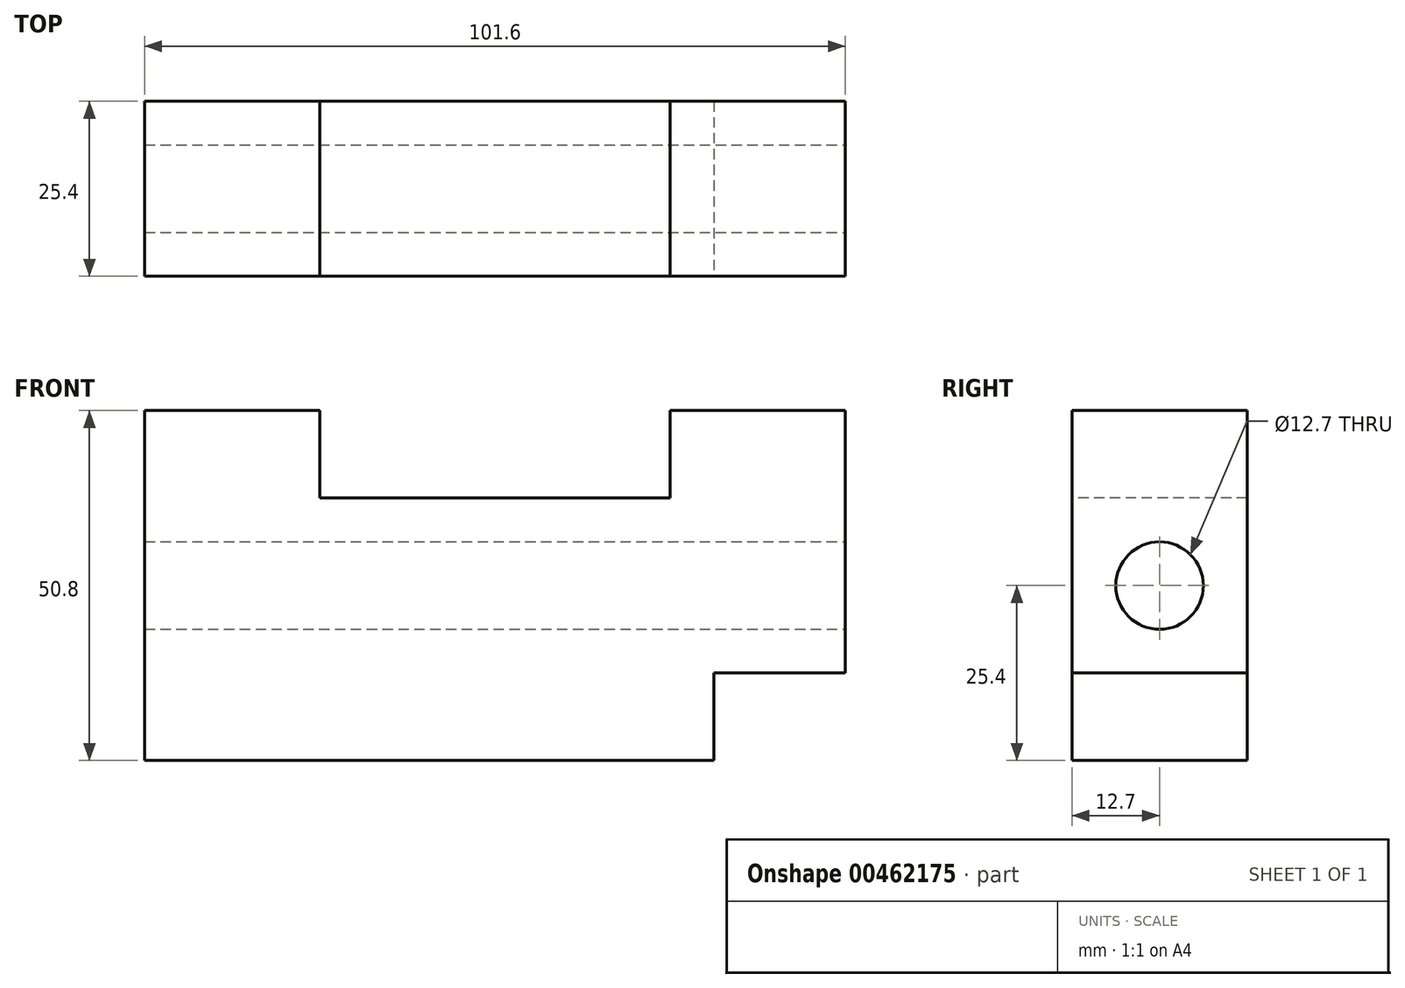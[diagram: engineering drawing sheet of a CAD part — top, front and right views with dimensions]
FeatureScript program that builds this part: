
annotation { "Feature Type Name" : "Feature", "Feature Type Description" : "" }
export const myFeature = defineFeature(function(context is Context, id is Id, definition is map)
    precondition{}
    {
        {
            var Q0;
            Q0=qCreatedBy(makeId("Front.planeOp"),FACE);
            var sketch = newSketch(context, id + "F0", { "sketchPlane" : qUnion([Q0])});
            skLineSegment(sketch, "E0.bottom", {"start": v(50.8, -25.4) * mm, "end": v(-50.8, -25.4) * mm});
            skLineSegment(sketch, "E0.top", {"start": v(50.8, 25.4) * mm, "end": v(-50.8, 25.4) * mm});
            skLineSegment(sketch, "E0.left", {"start": v(50.8, -25.4) * mm, "end": v(50.8, 25.4) * mm});
            skLineSegment(sketch, "E0.right", {"start": v(-50.8, -25.4) * mm, "end": v(-50.8, 25.4) * mm});
            skPoint(sketch, "E0.middle", {"position": v(0, 0) * mm});
            skSolve(sketch);
        }
        {
            var Q0;
            Q0 = qSketchRegion(id + "F0", true);
            extrude(context, id + "F1", {"entities" : qUnion([Q0]), "depth" : 25.4 * mm});
        }
        {
            var Q0;
            Q0=makeQuery(id+"F1.opExtrude","CAP_FACE",FACE,{"disambiguationData":[OSD([sQuery(id+"F0.wireOp",EDGE,"E0.bottom"),sQuery(id+"F0.wireOp",EDGE,"E0.top"),sQuery(id+"F0.wireOp",EDGE,"E0.left"),sQuery(id+"F0.wireOp",EDGE,"E0.right")])],"isStart":false});
            var sketch = newSketch(context, id + "F2", { "sketchPlane" : qUnion([Q0])});
            skLineSegment(sketch, "E1.bottom", {"start": v(50.8, -25.4) * mm, "end": v(31.75, -25.4) * mm});
            skLineSegment(sketch, "E1.top", {"start": v(50.8, -12.7) * mm, "end": v(31.75, -12.7) * mm});
            skLineSegment(sketch, "E1.left", {"start": v(50.8, -25.4) * mm, "end": v(50.8, -12.7) * mm});
            skLineSegment(sketch, "E1.right", {"start": v(31.75, -25.4) * mm, "end": v(31.75, -12.7) * mm});
            skSolve(sketch);
        }
        {
            var Q0;
            Q0=makeQuery(id+"F2.imprint","IMPRINT",FACE,{"disambiguationData":[TD([[makeQuery(id+"F2.imprint","IMPRINT",EDGE,{"derivedFrom":sQuery(id+"F2.wireOp",EDGE,"E1.bottom")}),-1.0]])]});
            var sketch = newSketch(context, id + "F3", { "sketchPlane" : qUnion([Q0])});
            skSolve(sketch);
        }
        {
            var Q0;
            Q0 = qSketchRegion(id + "F3", true);
            var Q1;
            Q1=makeQuery(id+"F2.imprint","IMPRINT",FACE,{"disambiguationData":[TD([[makeQuery(id+"F2.imprint","IMPRINT",EDGE,{"derivedFrom":sQuery(id+"F2.wireOp",EDGE,"E1.bottom")}),-1.0]])]});
            extrude(context, id + "F4", {"entities" : qUnion([Q0, Q1]), "operationType" : NewBodyOperationType.REMOVE, "oppositeDirection" : true, "depth" : 50.8 * mm});
        }
        {
            var Q0;
            Q0=makeQuery(id+"F1.opExtrude","CAP_FACE",FACE,{"disambiguationData":[OSD([sQuery(id+"F0.wireOp",EDGE,"E0.bottom"),sQuery(id+"F0.wireOp",EDGE,"E0.top"),sQuery(id+"F0.wireOp",EDGE,"E0.left"),sQuery(id+"F0.wireOp",EDGE,"E0.right")])],"isStart":false});
            var sketch = newSketch(context, id + "F5", { "sketchPlane" : qUnion([Q0])});
            skLineSegment(sketch, "E2.bottom", {"start": v(-25.4, 25.4) * mm, "end": v(25.4, 25.4) * mm});
            skLineSegment(sketch, "E2.top", {"start": v(-25.4, 12.7) * mm, "end": v(25.4, 12.7) * mm});
            skLineSegment(sketch, "E2.left", {"start": v(-25.4, 25.4) * mm, "end": v(-25.4, 12.7) * mm});
            skLineSegment(sketch, "E2.right", {"start": v(25.4, 25.4) * mm, "end": v(25.4, 12.7) * mm});
            skSolve(sketch);
        }
        {
            var Q0;
            Q0=makeQuery(id+"F5.imprint","IMPRINT",FACE,{"disambiguationData":[TD([[makeQuery(id+"F5.imprint","IMPRINT",EDGE,{"derivedFrom":sQuery(id+"F5.wireOp",EDGE,"E2.bottom")}),1.0]])]});
            extrude(context, id + "F6", {"entities" : qUnion([Q0]), "operationType" : NewBodyOperationType.REMOVE, "oppositeDirection" : true, "depth" : 25.4 * mm});
        }
        {
            var Q0;
            Q0=makeQuery(id+"F1.opExtrude","SWEPT_FACE",FACE,{"disambiguationData":[OSD([sQuery(id+"F0.wireOp",EDGE,"E0.left")])]});
            var sketch = newSketch(context, id + "F7", { "sketchPlane" : qUnion([Q0])});
            skCircle(sketch, "E3", {"center": v(-12.7, 0) * mm, "radius": 6.35 * mm});
            skSolve(sketch);
        }
        {
            var Q0;
            Q0=makeQuery(id+"F7.imprint","IMPRINT",FACE,{"disambiguationData":[TD([[makeQuery(id+"F7.imprint","IMPRINT",EDGE,{"derivedFrom":sQuery(id+"F7.wireOp",EDGE,"E3")}),1.0]])]});
            extrude(context, id + "F8", {"entities" : qUnion([Q0]), "operationType" : NewBodyOperationType.REMOVE, "oppositeDirection" : true, "depth" : 101.6 * mm});
        }
    });
